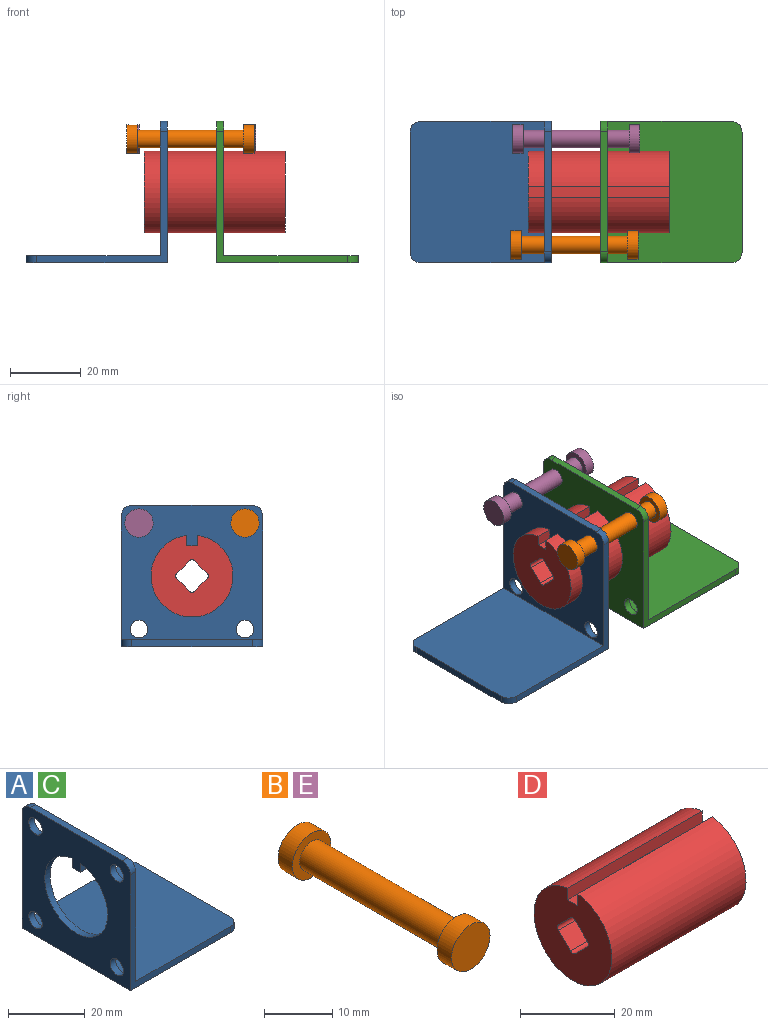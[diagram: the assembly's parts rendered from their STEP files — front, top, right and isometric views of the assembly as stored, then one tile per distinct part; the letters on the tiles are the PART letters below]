
ASSEMBLY  parts=5 mates=4
PART A: 20 faces, bbox 40x40x40 mm
  f0: plane 40x40mm, normal (-1,0,0), area 1103.8mm2, adj f2,f5,f6,f7,f8,f9,f10,f11
  f1: plane 40x38mm, normal (1,0,0), area 1023.8mm2, adj f4,f5,f6,f7,f8,f9,f10,f11
  f2: plane 40x40mm, normal (0,0,-1), area 1596.1mm2, adj f0,f3,f6,f7,f16,f18
  f3: plane 34x2mm, normal (1,0,0), area 68mm2, adj f2,f4,f16,f18
  f4: plane 40x38mm, normal (0,0,1), area 1516.1mm2, adj f1,f3,f6,f7,f16,f18
  f5: plane 34x2mm, normal (0,0,1), area 68mm2, adj f0,f1,f17,f19
  f6: plane 37x37mm, normal (0,-1,0), area 144mm2, adj f0,f1,f2,f4,f18,f19
  f7: plane 37x37mm, normal (0,1,0), area 144mm2, adj f0,f1,f2,f4,f16,f17
  f8: cylinder r=2.5mm len=5mm, axis (-1,0,0), area 31.4mm2, adj f0,f1
  f9: cylinder r=2.5mm len=5mm, axis (-1,0,0), area 31.4mm2, adj f0,f1
  f10: cylinder r=2.5mm len=5mm, axis (-1,0,0), area 31.4mm2, adj f0,f1
  f11: cylinder r=2.5mm len=5mm, axis (-1,0,0), area 31.4mm2, adj f0,f1
  f12: plane 3x2mm, normal (0,0,-1), area 6mm2, adj f0,f1,f13,f15
  f13: plane 3x2mm, normal (0,1,0), area 6mm2, adj f0,f1,f12,f14
  f14: cylinder r=11.6mm len=23.21mm, axis (-1,0,0), area 139.8mm2, adj f0,f1,f13,f15
  f15: plane 3x2mm, normal (0,-1,0), area 6mm2, adj f0,f1,f12,f14
  f16: cylinder r=3mm len=3mm, axis (0,0,1), area 9.4mm2, adj f2,f3,f4,f7
  f17: cylinder r=3mm len=3mm, axis (-1,0,0), area 9.4mm2, adj f0,f1,f5,f7
  f18: cylinder r=3mm len=3mm, axis (0,0,-1), area 9.4mm2, adj f2,f3,f4,f6
  f19: cylinder r=3mm len=3mm, axis (1,0,0), area 9.4mm2, adj f0,f1,f5,f6
PART B: 7 faces, bbox 8x36x8 mm
  f0: cylinder r=4mm len=8mm, axis (0,1,0), area 75.4mm2, adj f1,f2
  f1: plane 8x8mm, normal (0,-1,0), area 30.6mm2, adj f0,f3
  f2: plane 8x8mm, normal (0,1,0), area 50.3mm2, adj f0
  f3: cylinder r=2.5mm len=30mm, axis (0,1,0), area 471.2mm2, adj f1,f6
  f4: cylinder r=4mm len=8mm, axis (0,1,0), area 75.4mm2, adj f5,f6
  f5: plane 8x8mm, normal (0,-1,0), area 50.3mm2, adj f4
  f6: plane 8x8mm, normal (0,1,0), area 30.6mm2, adj f3,f4
PART C: same geometry as A
PART D: 14 faces, bbox 40x23.2x23.1 mm
  f0: plane 23.21x23.11mm, normal (1,0,0), area 364.6mm2, adj f2,f3,f4,f5,f6,f7,f8,f9
  f1: plane 23.21x23.11mm, normal (-1,0,0), area 364.6mm2, adj f2,f3,f4,f5,f6,f7,f8,f9
  f2: plane 40x3mm, normal (0,-1,0), area 120mm2, adj f0,f1,f3,f5
  f3: plane 40x3mm, normal (0,0,1), area 120mm2, adj f0,f1,f2,f4
  f4: plane 40x3mm, normal (0,1,0), area 120mm2, adj f0,f1,f3,f5
  f5: cylinder r=11.6mm len=40mm, axis (-1,0,0), area 2795.9mm2, adj f0,f1,f2,f4
  f6: plane 40x3.59mm, normal (0,0.71,-0.71), area 202.8mm2, adj f0,f1,f10,f13
  f7: plane 40x3.59mm, normal (0,-0.71,-0.71), area 202.8mm2, adj f0,f1,f10,f11
  f8: plane 40x3.59mm, normal (0,-0.71,0.71), area 202.8mm2, adj f0,f1,f11,f12
  f9: plane 40x3.59mm, normal (0,0.71,0.71), area 202.8mm2, adj f0,f1,f12,f13
  f10: cylinder r=1mm len=40mm, axis (-1,0,0), area 62.8mm2, adj f0,f1,f6,f7
  f11: cylinder r=1mm len=40mm, axis (-1,0,0), area 62.8mm2, adj f0,f1,f7,f8
  f12: cylinder r=1mm len=40mm, axis (-1,0,0), area 62.8mm2, adj f0,f1,f8,f9
  f13: cylinder r=1mm len=40mm, axis (-1,0,0), area 62.8mm2, adj f0,f1,f6,f9
PART E: same geometry as B
PLACE A rot(axis=(0,0,-1),180deg) t=(39.72,23.12,-37.8)mm fixed
PLACE B rot(axis=(0,0,1),90deg) t=(28.24,28.12,-2.8)mm
PLACE C t=(53.66,63.12,-37.8)mm fixed
PLACE D t=(33.12,43.12,-12.63)mm
PLACE E rot(axis=(0,0,1),90deg) t=(28.74,58.12,-2.8)mm
MATE slider C.f14 <-> D.f5  axis (-1,0,0) through (54.66,43.12,-17.8)mm
MATE slider D.f5 <-> A.f14  axis (-1,0,0) through (53.12,43.12,-17.8)mm
MATE slider B.f3 <-> C.f11  axis (-1,0,0) through (46.24,28.12,-2.8)mm
MATE slider E.f3 <-> C.f9  axis (-1,0,0) through (46.74,58.12,-2.8)mm
